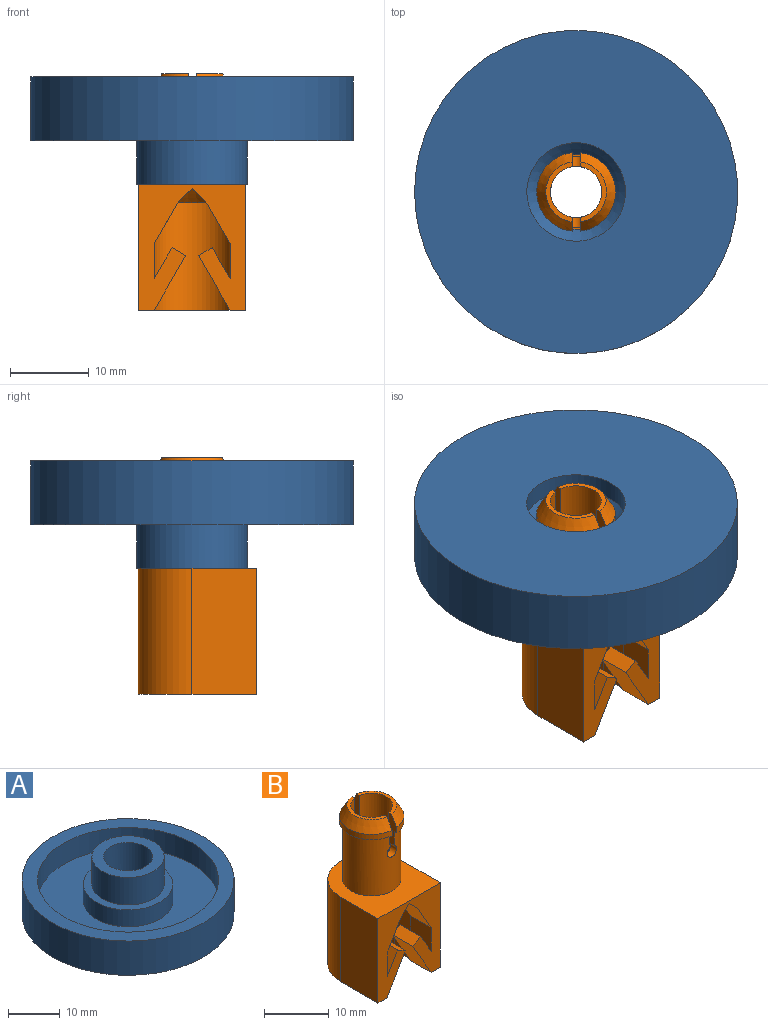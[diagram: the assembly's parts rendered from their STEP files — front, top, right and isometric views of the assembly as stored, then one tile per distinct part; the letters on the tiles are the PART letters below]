
ASSEMBLY  parts=2 mates=1
PART A: 12 faces, bbox 41x41x13.6 mm
  f0: cylinder r=4.75mm len=9.6mm, axis (0,0,1), area 286.5mm2, adj f9,f11
  f1: cylinder r=20.5mm len=41mm, axis (0,0,-1), area 1043.3mm2, adj f2,f3
  f2: plane 41x41mm, normal (0,0,1), area 358.1mm2, adj f1,f4
  f3: plane 41x41mm, normal (0,0,-1), area 1197.5mm2, adj f1,f10
  f4: cylinder r=17.5mm len=35mm, axis (0,0,1), area 549.8mm2, adj f2,f5
  f5: plane 35x35mm, normal (0,0,1), area 727.1mm2, adj f4,f6
  f6: cylinder r=8.65mm len=17.3mm, axis (0,0,-1), area 217.4mm2, adj f5,f7
  f7: plane 17.3x17.3mm, normal (0,0,1), area 81.1mm2, adj f6,f8
  f8: cylinder r=7mm len=14mm, axis (0,0,-1), area 285.9mm2, adj f7,f9
  f9: plane 14x14mm, normal (0,0,1), area 83.1mm2, adj f0,f8
  f10: cylinder r=6.25mm len=12.5mm, axis (0,0,-1), area 98.2mm2, adj f3,f11
  f11: cone r=4.75mm half-angle=45deg, axis (0,0,-1), area 73.3mm2, adj f0,f10
PART B: 42 faces, bbox 13.7x15x30 mm
  f0: plane 16x13.63mm, normal (0,-1,0), area 123.7mm2, adj f6,f8,f9,f10,f17,f18,f19,f20
  f1: plane 2.98x1.55mm, normal (0,0,-1), area 1.7mm2, adj f28,f29,f39
  f2: cylinder r=5mm len=9.95mm, axis (0,0,-1), area 14.7mm2, adj f3,f4,f33,f38
  f3: plane 9.95x4.5mm, normal (0,0,-1), area 7mm2, adj f2,f11,f33,f38
  f4: cone r=5mm half-angle=30deg, axis (0,0,-1), area 29.7mm2, adj f2,f5,f33,f38
  f5: plane 7.63x3.35mm, normal (0,0,1), area 6mm2, adj f4,f16,f33,f38
  f6: plane 15x13.63mm, normal (0,0,-1), area 65.1mm2, adj f0,f7,f8,f9,f17,f18,f28,f29
  f7: cylinder r=6.81mm len=16mm, axis (0,0,-1), area 342.6mm2, adj f6,f8,f9,f10
  f8: plane 16x8.19mm, normal (-1,0,0), area 131mm2, adj f0,f6,f7,f10
  f9: plane 16x8.19mm, normal (1,0,0), area 131mm2, adj f0,f6,f7,f10
  f10: plane 15x13.63mm, normal (0,0,1), area 120.9mm2, adj f0,f7,f8,f9,f11
  f11: cylinder r=4.5mm len=11mm, axis (0,0,-1), area 299.6mm2, adj f3,f10,f13,f33,f34,f35,f36,f37
  f12: cylinder r=5mm len=9.95mm, axis (0,0,-1), area 14.7mm2, adj f13,f14,f35,f36
  f13: plane 9.95x4.5mm, normal (0,0,-1), area 7mm2, adj f11,f12,f35,f36
  f14: cone r=5mm half-angle=30deg, axis (0,0,-1), area 29.7mm2, adj f12,f15,f35,f36
  f15: plane 7.63x3.35mm, normal (0,0,1), area 6mm2, adj f14,f16,f35,f36
  f16: cylinder r=3.25mm len=14.6mm, axis (0,0,1), area 280.6mm2, adj f5,f15,f33,f34,f35,f36,f37,f38
  f17: plane 6.93x4.5mm, normal (0.87,0,-0.5), area 36mm2, adj f0,f6,f27,f28
  f18: plane 6.93x4.5mm, normal (-0.87,0,-0.5), area 36mm2, adj f0,f6,f19,f30
  f19: plane 4.5x1.73mm, normal (-0.5,0,0.87), area 9mm2, adj f0,f18,f20,f30
  f20: plane 4.5x3.93mm, normal (0.87,0,0.5), area 20.4mm2, adj f0,f19,f21,f30
  f21: plane 4.5x4.5mm, normal (-1,0,0), area 20.2mm2, adj f0,f20,f22,f30
  f22: plane 6.31x4.54mm, normal (-0.87,0,-0.5), area 27.2mm2, adj f0,f21,f30,f39,f41
  f23: plane 2.98x1.55mm, normal (0,0,-1), area 1.7mm2, adj f30,f32,f39
  f24: plane 6.31x4.54mm, normal (0.87,0,-0.5), area 27.2mm2, adj f0,f25,f28,f39,f40
  f25: plane 4.5x4.5mm, normal (1,0,0), area 20.2mm2, adj f0,f24,f26,f28
  f26: plane 4.5x3.93mm, normal (-0.87,0,0.5), area 20.4mm2, adj f0,f25,f27,f28
  f27: plane 4.5x1.73mm, normal (0.5,0,0.87), area 9mm2, adj f0,f17,f26,f28
  f28: plane 14.78x4.19mm, normal (0,1,0), area 23.7mm2, adj f1,f6,f17,f24,f25,f26,f27,f29
  f29: plane 13.69x3.72mm, normal (1,0,0), area 50.1mm2, adj f1,f6,f28,f31,f39
  f30: plane 14.78x4.19mm, normal (0,1,0), area 23.7mm2, adj f6,f18,f19,f20,f21,f22,f23,f32
  f31: cylinder r=5mm len=13.65mm, axis (0,0,-1), area 214.4mm2, adj f6,f29,f32,f39
  f32: plane 13.69x3.72mm, normal (-1,0,0), area 50.1mm2, adj f6,f23,f30,f31,f39
  f33: plane 5.65x1.78mm, normal (-1,0,0), area 7.5mm2, adj f2,f3,f4,f5,f11,f16,f34
  f34: cylinder r=1mm len=2mm, axis (0,-1,0), area 6.7mm2, adj f11,f16,f33,f35
  f35: plane 5.65x1.78mm, normal (1,0,0), area 7.5mm2, adj f11,f12,f13,f14,f15,f16,f34
  f36: plane 5.65x1.78mm, normal (1,0,0), area 7.5mm2, adj f11,f12,f13,f14,f15,f16,f37
  f37: cylinder r=1mm len=2mm, axis (0,-1,0), area 6.7mm2, adj f11,f16,f36,f38
  f38: plane 5.65x1.78mm, normal (-1,0,0), area 7.5mm2, adj f2,f3,f4,f5,f11,f16,f37
  f39: cone r=5.05mm half-angle=45deg, axis (0,0,-1), area 56.6mm2, adj f1,f16,f22,f23,f24,f28,f29,f30
  f40: plane 4.94x1.87mm, normal (0.71,0,-0.71), area 11.1mm2, adj f0,f16,f24,f39,f41
  f41: plane 4.94x1.87mm, normal (-0.71,0,-0.71), area 11.1mm2, adj f0,f16,f22,f39,f40
PLACE A rot(axis=(0,-1,0),180deg) t=(-21.97,2.2,12.31)mm
PLACE B t=(-21.97,2.2,-17.29)mm
MATE fastened B.f11 <-> A.f0  axis (0,0,-1) through (-21.97,2.2,-1.29)mm
